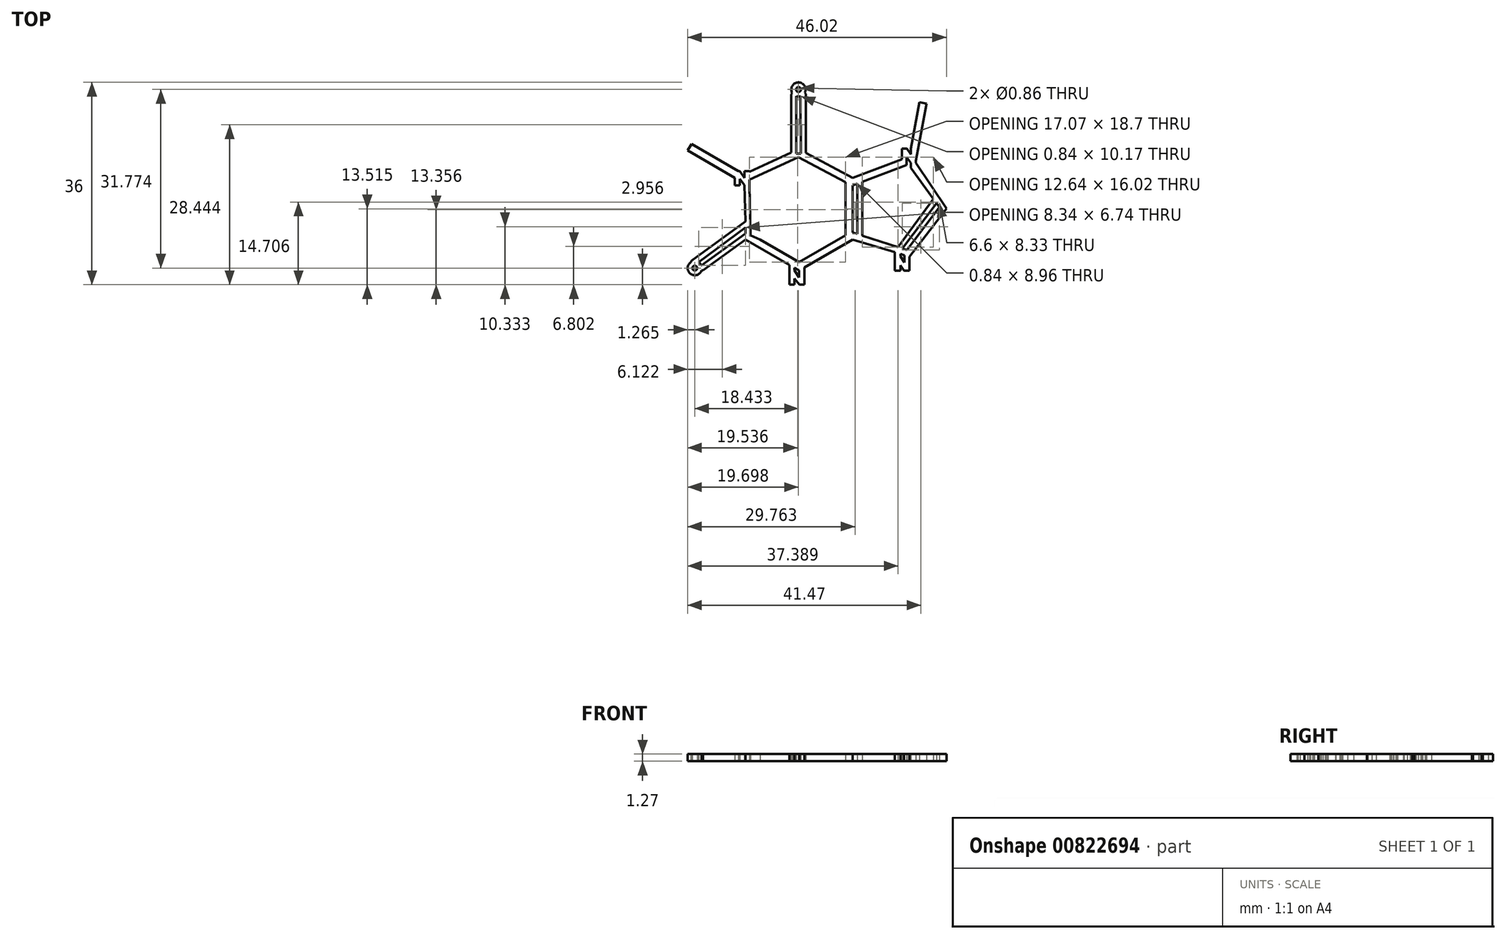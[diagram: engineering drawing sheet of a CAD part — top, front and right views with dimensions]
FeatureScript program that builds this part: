
annotation { "Feature Type Name" : "Feature", "Feature Type Description" : "" }
export const myFeature = defineFeature(function(context is Context, id is Id, definition is map)
    precondition{}
    {
        {
            var Q0;
            Q0=qCreatedBy(makeId("Top.planeOp"),FACE);
            var sketch = newSketch(context, id + "F0", { "sketchPlane" : qUnion([Q0])});
            skLineSegment(sketch, "E0.0", {"start": v(4.32, 2.26) * mm, "end": v(12.65, -2.15) * mm});
            skLineSegment(sketch, "E0.2", {"start": v(12.65, -13.15) * mm, "end": v(4.04, -18.13) * mm});
            skLineSegment(sketch, "E0.3", {"start": v(3.13, -18.65) * mm, "end": v(2.29, -18.17) * mm});
            skLineSegment(sketch, "E1.1", {"start": v(11.38, -2.92) * mm, "end": v(11.38, -3.77) * mm});
            skLineSegment(sketch, "E1.2", {"start": v(11.38, -12.42) * mm, "end": v(3.13, -17.19) * mm});
            skLineSegment(sketch, "E1.3", {"start": v(3, 1.52) * mm, "end": v(11.38, -2.92) * mm});
            skLineSegment(sketch, "E1.4", {"start": v(3.13, -17.19) * mm, "end": v(2.03, -16.55) * mm});
            skLineSegment(sketch, "E2.trimOffspring", {"start": v(11.38, -4.8) * mm, "end": v(11.38, -10.51) * mm});
            skLineSegment(sketch, "E3.trimOffspring", {"start": v(11.38, -11.54) * mm, "end": v(11.38, -12.42) * mm});
            skLineSegment(sketch, "E4.trimOffspring", {"start": v(1.14, -16.04) * mm, "end": v(-3.8, -13.18) * mm});
            skLineSegment(sketch, "E5", {"start": v(-6.4, -13.15) * mm, "end": v(-13.97, -18.65) * mm});
            skLineSegment(sketch, "E6.0", {"start": v(-6.4, -9.92) * mm, "end": v(-16.03, -16.92) * mm});
            skCircle(sketch, "E7", {"center": v(-15.42, -18.23) * mm, "radius": 0.43 * mm});
            skLineSegment(sketch, "E8", {"start": v(11.38, -2.92) * mm, "end": v(11.38, -12.42) * mm});
            skLineSegment(sketch, "E9", {"start": v(3, 1.52) * mm, "end": v(-5.31, -2.3) * mm});
            skLineSegment(sketch, "E10", {"start": v(-3.8, -13.18) * mm, "end": v(3.13, -17.19) * mm});
            skLineSegment(sketch, "E11", {"start": v(-16.68, 2.74) * mm, "end": v(-16.02, 3.88) * mm});
            skLineSegment(sketch, "E12.0", {"start": v(23, -0.41) * mm, "end": v(27.02, -5.94) * mm});
            skLineSegment(sketch, "E12.1", {"start": v(12.65, -3.51) * mm, "end": v(13.5, -3.2) * mm});
            skLineSegment(sketch, "E12.2", {"start": v(28.08, -7.4) * mm, "end": v(22.32, -15.02) * mm});
            skLineSegment(sketch, "E12.3", {"start": v(22.32, -15.02) * mm, "end": v(21.48, -14.75) * mm});
            skLineSegment(sketch, "E12.4", {"start": v(12.65, -11.88) * mm, "end": v(12.65, -3.51) * mm});
            skLineSegment(sketch, "E13", {"start": v(13.5, -3.2) * mm, "end": v(13.5, -12.15) * mm});
            skLineSegment(sketch, "E14", {"start": v(14.38, -12.44) * mm, "end": v(14.38, -2.86) * mm});
            skLineSegment(sketch, "E15", {"start": v(27.56, -6.69) * mm, "end": v(21.48, -14.75) * mm});
            skLineSegment(sketch, "E16", {"start": v(20.69, -14.5) * mm, "end": v(27.02, -5.94) * mm});
            skLineSegment(sketch, "E17.trimOffspring", {"start": v(14.38, -2.86) * mm, "end": v(22.26, 0.1) * mm});
            skLineSegment(sketch, "E18.trimOffspring", {"start": v(13.5, -12.15) * mm, "end": v(12.65, -11.88) * mm});
            skLineSegment(sketch, "E19.trimOffspring", {"start": v(27.56, -6.69) * mm, "end": v(28.08, -7.4) * mm});
            skLineSegment(sketch, "E20.trimOffspring", {"start": v(20.69, -14.5) * mm, "end": v(14.38, -12.44) * mm});
            skLineSegment(sketch, "E21.left", {"start": v(21.38, 3.03) * mm, "end": v(21.38, 1.13) * mm});
            skLineSegment(sketch, "E21.right", {"start": v(22.26, 1.52) * mm, "end": v(22.26, 0.49) * mm});
            skLineSegment(sketch, "E22", {"start": v(21.38, 3.03) * mm, "end": v(22.27, 3.03) * mm});
            skLineSegment(sketch, "E23", {"start": v(22.27, 3.03) * mm, "end": v(23, 2) * mm});
            skLineSegment(sketch, "E24", {"start": v(23, 2) * mm, "end": v(23, 3.03) * mm});
            skLineSegment(sketch, "E25", {"start": v(23, 3.03) * mm, "end": v(23.9, 3.03) * mm});
            skLineSegment(sketch, "E26", {"start": v(23.9, 3.03) * mm, "end": v(23.9, 0.49) * mm});
            skLineSegment(sketch, "E27", {"start": v(22.26, 1.52) * mm, "end": v(23, 0.49) * mm});
            skLineSegment(sketch, "E28.left", {"start": v(20.12, -16.18) * mm, "end": v(20.12, -18.72) * mm});
            skLineSegment(sketch, "E28.right", {"start": v(21.14, -17.75) * mm, "end": v(21.14, -18.72) * mm});
            skLineSegment(sketch, "E29", {"start": v(21.14, -16.18) * mm, "end": v(21.87, -17.24) * mm});
            skLineSegment(sketch, "E30", {"start": v(21.87, -17.24) * mm, "end": v(21.87, -16.18) * mm});
            skLineSegment(sketch, "E31", {"start": v(22.76, -16.22) * mm, "end": v(22.76, -18.72) * mm});
            skLineSegment(sketch, "E32", {"start": v(21.14, -17.75) * mm, "end": v(21.8, -18.72) * mm});
            skLineSegment(sketch, "E33", {"start": v(12.65, -2.15) * mm, "end": v(21.38, 1.13) * mm});
            skLineSegment(sketch, "E34", {"start": v(23.9, 0.49) * mm, "end": v(29.33, -7.62) * mm});
            skLineSegment(sketch, "E35", {"start": v(29.33, -7.62) * mm, "end": v(22.76, -16.22) * mm});
            skLineSegment(sketch, "E36", {"start": v(12.65, -13.15) * mm, "end": v(20.12, -15.42) * mm});
            skLineSegment(sketch, "E37", {"start": v(-16.68, 2.74) * mm, "end": v(-8.33, -2.19) * mm});
            skLineSegment(sketch, "E38", {"start": v(-16.02, 3.88) * mm, "end": v(-7.65, -0.97) * mm});
            skLineSegment(sketch, "E39", {"start": v(-6.58, -3.44) * mm, "end": v(-6.4, -9.92) * mm});
            skLineSegment(sketch, "E40", {"start": v(20.12, -16.18) * mm, "end": v(20.12, -15.42) * mm});
            skLineSegment(sketch, "E41", {"start": v(21.14, -16.18) * mm, "end": v(21.14, -15.72) * mm});
            skLineSegment(sketch, "E42", {"start": v(21.87, -16.18) * mm, "end": v(21.87, -15.95) * mm});
            skLineSegment(sketch, "E43.trimOffspring", {"start": v(21.14, -15.72) * mm, "end": v(21.87, -15.95) * mm});
            skLineSegment(sketch, "E44", {"start": v(20.12, -18.72) * mm, "end": v(21.14, -18.72) * mm});
            skLineSegment(sketch, "E45", {"start": v(21.8, -18.72) * mm, "end": v(22.76, -18.72) * mm});
            skLineSegment(sketch, "E46.left", {"start": v(1.4, -18.65) * mm, "end": v(1.4, -21.2) * mm});
            skLineSegment(sketch, "E46.right", {"start": v(2.29, -20.06) * mm, "end": v(2.29, -21.2) * mm});
            skLineSegment(sketch, "E47", {"start": v(2.29, -18.65) * mm, "end": v(3.13, -19.88) * mm});
            skLineSegment(sketch, "E48", {"start": v(3.13, -19.88) * mm, "end": v(3.13, -18.65) * mm});
            skLineSegment(sketch, "E49", {"start": v(4.04, -18.65) * mm, "end": v(4.04, -21.2) * mm});
            skLineSegment(sketch, "E50", {"start": v(2.29, -20.06) * mm, "end": v(3.2, -21.19) * mm});
            skLineSegment(sketch, "E51", {"start": v(1.4, -21.2) * mm, "end": v(2.29, -21.2) * mm});
            skLineSegment(sketch, "E52", {"start": v(3.2, -21.19) * mm, "end": v(4.04, -21.2) * mm});
            skLineSegment(sketch, "E53", {"start": v(1.4, -18.65) * mm, "end": v(1.4, -17.65) * mm});
            skLineSegment(sketch, "E54", {"start": v(4.04, -18.65) * mm, "end": v(4.04, -18.13) * mm});
            skLineSegment(sketch, "E55", {"start": v(2.29, -18.65) * mm, "end": v(2.29, -18.17) * mm});
            skLineSegment(sketch, "E56.trimOffspring", {"start": v(1.4, -17.65) * mm, "end": v(-6.4, -13.15) * mm});
            skLineSegment(sketch, "E57.left", {"start": v(-8.33, -0.97) * mm, "end": v(-8.33, -3.51) * mm});
            skLineSegment(sketch, "E57.right", {"start": v(-7.44, -2.38) * mm, "end": v(-7.44, -3.51) * mm});
            skLineSegment(sketch, "E58", {"start": v(-7.44, -0.97) * mm, "end": v(-6.58, -2.2) * mm});
            skLineSegment(sketch, "E59", {"start": v(-6.58, -2.2) * mm, "end": v(-6.58, -0.97) * mm});
            skLineSegment(sketch, "E60", {"start": v(-5.7, -0.97) * mm, "end": v(-5.7, -3.51) * mm});
            skLineSegment(sketch, "E61", {"start": v(-7.44, -2.38) * mm, "end": v(-6.52, -3.51) * mm});
            skLineSegment(sketch, "E62", {"start": v(-8.33, -3.51) * mm, "end": v(-7.44, -3.51) * mm});
            skLineSegment(sketch, "E63", {"start": v(-6.52, -3.51) * mm, "end": v(-5.7, -3.51) * mm});
            skLineSegment(sketch, "E64", {"start": v(-8.33, -0.97) * mm, "end": v(-7.44, -0.97) * mm});
            skLineSegment(sketch, "E65", {"start": v(-6.58, -0.97) * mm, "end": v(-5.7, -0.97) * mm});
            skLineSegment(sketch, "E66.trimOffspring", {"start": v(-5.7, -1.1) * mm, "end": v(1.7, 2.3) * mm});
            skLineSegment(sketch, "E67", {"start": v(24.53, 11.27) * mm, "end": v(25.78, 11.04) * mm});
            skLineSegment(sketch, "E68", {"start": v(24.53, 11.27) * mm, "end": v(23, 3.03) * mm});
            skLineSegment(sketch, "E69", {"start": v(25.78, 11.04) * mm, "end": v(23.9, 0.85) * mm});
            skLineSegment(sketch, "E70", {"start": v(-6.4, -11.02) * mm, "end": v(-6.4, -12.05) * mm});
            skLineSegment(sketch, "E71", {"start": v(-6.4, -12.05) * mm, "end": v(-14.25, -17.76) * mm});
            skLineSegment(sketch, "E72", {"start": v(-14.74, -17.16) * mm, "end": v(-6.4, -11.02) * mm});
            skArc(sketch, "E73", {"start": v(-16.1, -17.16) * mm, "mid": v(-16.21, -19.23) * mm, "end": v(-14.23, -18.65) * mm});
            skLineSegment(sketch, "E74", {"start": v(-16.03, -16.92) * mm, "end": v(-16.1, -17.16) * mm});
            skLineSegment(sketch, "E75", {"start": v(-13.97, -18.65) * mm, "end": v(-14.23, -18.65) * mm});
            skArc(sketch, "E76.trimOffspring", {"start": v(-14.25, -17.76) * mm, "mid": v(-14.45, -17.42) * mm, "end": v(-14.74, -17.16) * mm});
            skLineSegment(sketch, "E77", {"start": v(1.7, 2.3) * mm, "end": v(1.71, 12.66) * mm});
            skLineSegment(sketch, "E78.0", {"start": v(4.32, 2.26) * mm, "end": v(4.33, 12.76) * mm});
            skCircle(sketch, "E79", {"center": v(3, 13.54) * mm, "radius": 0.43 * mm});
            skLineSegment(sketch, "E80", {"start": v(3.43, 2.17) * mm, "end": v(2.59, 2.17) * mm});
            skLineSegment(sketch, "E81", {"start": v(2.59, 2.17) * mm, "end": v(2.6, 12.34) * mm});
            skLineSegment(sketch, "E82", {"start": v(3.4, 12.33) * mm, "end": v(3.43, 2.17) * mm});
            skPoint(sketch, "E83", {"position": v(3, 2.17) * mm});
            skLineSegment(sketch, "E84", {"start": v(22.26, 0.49) * mm, "end": v(22.26, 0.1) * mm});
            skLineSegment(sketch, "E85", {"start": v(23, -0.41) * mm, "end": v(23, 0.49) * mm});
            skPoint(sketch, "E86.start.orphan", {"position": v(21.38, 0.49) * mm});
            skPoint(sketch, "E87.endSnap0", {"position": v(-5.7, -2.24) * mm});
            skLineSegment(sketch, "E88", {"start": v(-5.7, -3.51) * mm, "end": v(-5.53, -12.42) * mm});
            skLineSegment(sketch, "E89", {"start": v(-5.31, -2.3) * mm, "end": v(-5.7, -2.48) * mm});
            skPoint(sketch, "E87.end.orphan", {"position": v(-5.7, -2.3) * mm});
            skLineSegment(sketch, "E90", {"start": v(-3.8, -13.18) * mm, "end": v(-5.53, -12.42) * mm});
            skPoint(sketch, "E91.orphan", {"position": v(-5.13, -12.42) * mm});
            skArc(sketch, "E92", {"start": v(2.6, 12.34) * mm, "mid": v(3, 12.27) * mm, "end": v(3.4, 12.33) * mm});
            skLineSegment(sketch, "E93", {"start": v(1.71, 12.66) * mm, "end": v(1.9, 12.92) * mm});
            skLineSegment(sketch, "E94", {"start": v(4.33, 12.76) * mm, "end": v(4.16, 13) * mm});
            skArc(sketch, "E95.trimOffspring", {"start": v(4.16, 13) * mm, "mid": v(2.96, 14.8) * mm, "end": v(1.9, 12.92) * mm});
            skSolve(sketch);
        }
        {
            var Q0;
            Q0=makeQuery(id+"F0.imprint","IMPRINT",FACE,{"disambiguationData":[TD([[makeQuery(id+"F0.imprint","IMPRINT",EDGE,{"derivedFrom":sQuery(id+"F0.wireOp",EDGE,"E0.0")}),-1.0]])]});
            var Q1;
            Q1=makeQuery(id+"F0.imprint","IMPRINT",FACE,{"disambiguationData":[TD([[makeQuery(id+"F0.imprint","IMPRINT",EDGE,{"derivedFrom":sQuery(id+"F0.wireOp",EDGE,"E11")}),-1.0]])]});
            var Q2;
            {var subQ4=sQuery(id+"F0.wireOp",EDGE,"E57.right");Q2=makeQuery(id+"F0.imprint","IMPRINT",FACE,{"disambiguationData":[TD([[makeQuery(id+"F0.imprint","IMPRINT",EDGE,{"derivedFrom":subQ4}),-1.0]])]});}
            var Q3;
            Q3=makeQuery(id+"F0.imprint","IMPRINT",FACE,{"disambiguationData":[TD([[makeQuery(id+"F0.imprint","IMPRINT",EDGE,{"derivedFrom":sQuery(id+"F0.wireOp",EDGE,"E21.right")}),-1.0]])]});
            var Q4;
            {var subQ1=sQuery(id+"F0.wireOp",EDGE,"E25");Q4=makeQuery(id+"F0.imprint","IMPRINT",FACE,{"disambiguationData":[TD([[makeQuery(id+"F0.imprint","IMPRINT",EDGE,{"derivedFrom":subQ1}),1.0]])]});}
            extrude(context, id + "F1", {"entities" : qUnion([Q0, Q1, Q2, Q3, Q4]), "depth" : 1.27 * mm, "offsetDistance" : 25.4 * mm});
        }
    });
